# Revit family: Hager-Volta-IP30-Hollow_wall-sistema-NoHosted-CH-it
name_source: partatom
category: Electrical Equipment
units: mm (PartAtom-declared; Revit-internal decimal feet)

## family parameters
Always vertical = Yes
Cut with Voids When Loaded = No
Panel Configuration = Two Columns, Circuits Across
Part Type = Panelboard
Room Calculation Point = No
Round Connector Dimension = Use Diameter
Shared = No
Work Plane-Based = Yes

## types (6) — shared parameters
Default Elevation = 1219 mm
EF000003 - Tipo di montaggio = EV000128 - parete forata
EF000007 - colore = EV000202 - bianco
EF000008 - Larghezza = 348 mm  [stored 1.14173 ft]
EF000049 - profondità = 98 mm  [stored 0.321522 ft]
EF000116 - numero RAL = 9010
EF000118 - con piastra di montaggio = No
EF000218 - profondità di incasso = 89 mm  [stored 0.291995 ft]
EF000339 - tipo di copertura = EV004216 - porta
EF000846 - larghezza di montaggio = 314 mm  [stored 1.03018 ft]
EF001062 - esecuzione EMC = No
EF001088 - possibilità di applicazione = Yes
EF001131 - profondità interna = 92 mm
EF001134 - barra DIN = Yes
EF002950 - Numero moduli DIN = 12
EF004462 - tipo di chiusura = EV000154 - altri
EF005474 - grado di protezione (IP) = EV006410 - IP30
EF006244 - coperchio/porta trasparente = No
EF006306 - con serratura = No
EF009212 - esecuzione coperchio = EV009916 - con taglio
EF015777 - Morsettiera neutra = No
EF015941 - Segnale di passaggio porta = No
HG000001 - Numero di colonne = 1
HG000002 - Con porta = Yes
HG000003 - Gamma = Volta
HG000005 - Spessore = 3 mm  [stored 0.00984252 ft]
HG000006 - Ad incasso = Yes
HG000009 - Porta doppia a battente = No
HG000010 - Porte asimmetriche = No
HG000011 - File vuote nella parte basse = No
HG000017 - Distanza tra i poli = 18 mm  [stored 0.0590551 ft]
Manufacturer = Hager
Type Comments = Volta
zero-valued in all types: HG000007 - Numero di colonne vuote, HG000008 - Numero di file vuote

## per-type parameters (varying)
| type | EF000040 - Altezza | EF000266 - numero di file | EF000332 - Altezza della parte incassata | EF001596 - Attacco Lampada | EF015776 - Morsettiera di terra | HG000004 - Codice produttore | Model |
| incassato IP30 L348 A356.5 P98 12 Unità di divisione - VH12NA | 356 mm | 1 | 321 mm | EV000139 - plastica | Yes | VH12NA | VH12NA |
| incassato IP30 L348 A505.5 P98 12 Unità di divisione - VH24NA | 506 mm | 2 | 470 mm | EV000139 - plastica | Yes | VH24NA | VH24NA |
| incassato IP30 L348 A630.5 P98 12 Unità di divisione - VH36NA | 630 mm | 3 | 595 mm | EV000139 - plastica | Yes | VH36NA | VH36NA |
| incassato IP30 L348 A755.5 P98 12 Unità di divisione - VH48NA | 756 mm | 4 | 720 mm  [stored 2.3622 ft] | EV000139 - plastica | Yes | VH48NA | VH48NA |
| incassato IP30 L348 A755.5 P98 12 Unità di divisione - VH48NRM | 756 mm | 4 | 720 mm  [stored 2.3622 ft] | EV000139 - plastica | No | VH48NRM | VH48NRM |
| incassato IP30 L348 A880.5 P98 12 Unità di divisione - VH60NA | 880 mm  [stored 2.88714 ft] | 5 | 845 mm  [stored 2.77231 ft] | EV000154 - altri | Yes | VH60NA | VH60NA |

note: [stored X ft] marks values corroborated as IEEE doubles in the binary element streams (Revit-internal decimal feet)

## geometry (parser evidence)
native form markers: Sweep x13
no freeform markers — native parametric forms only
